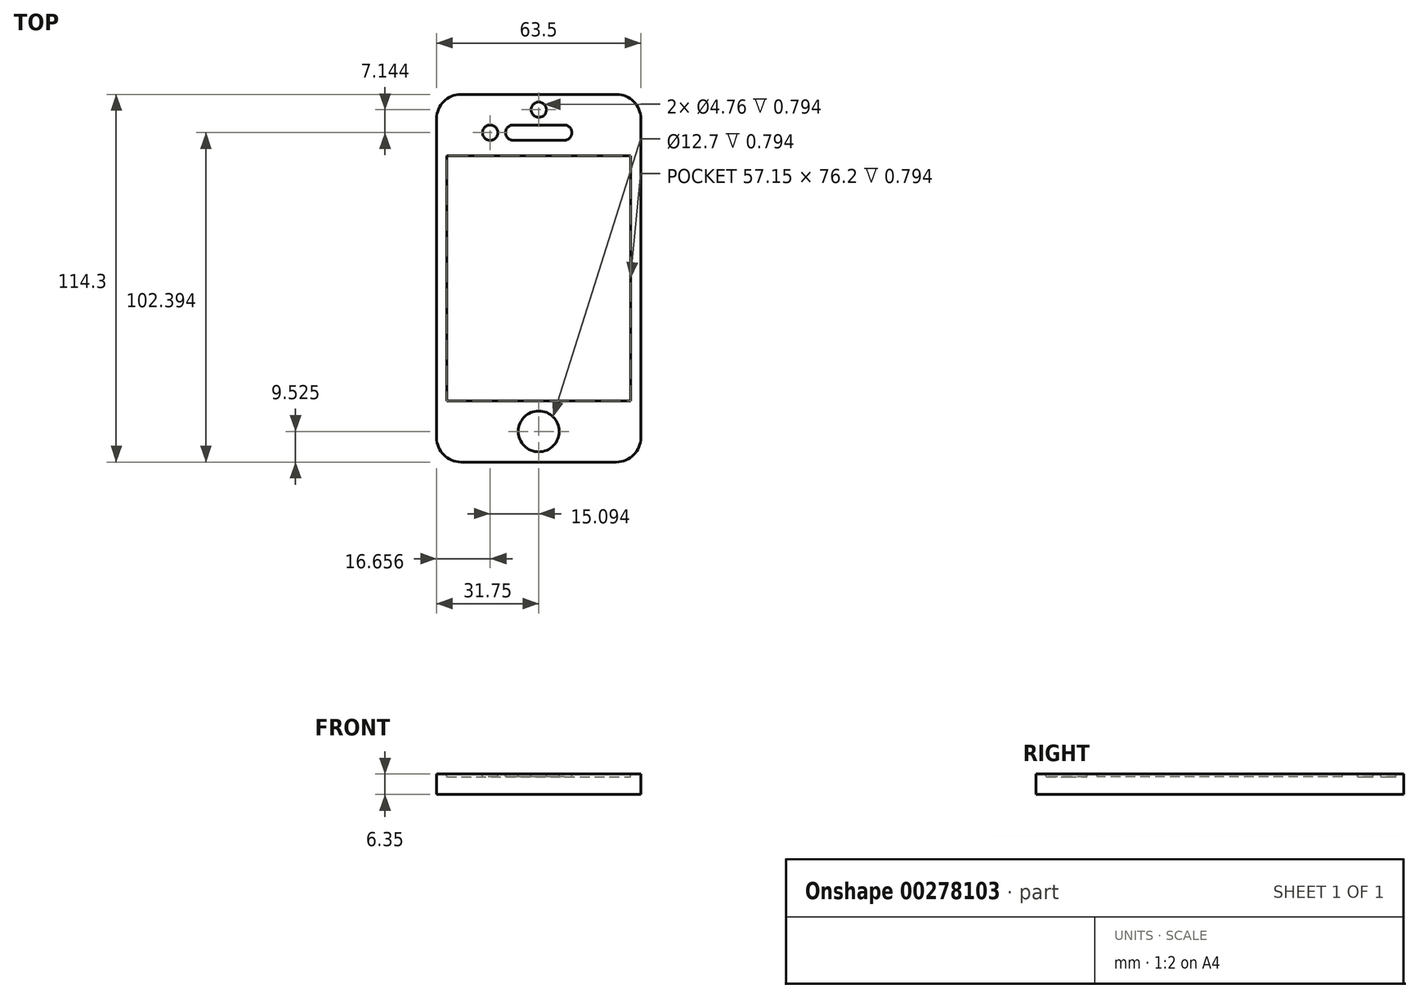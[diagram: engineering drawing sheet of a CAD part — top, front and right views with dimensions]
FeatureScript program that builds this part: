
annotation { "Feature Type Name" : "Feature", "Feature Type Description" : "" }
export const myFeature = defineFeature(function(context is Context, id is Id, definition is map)
    precondition{}
    {
        {
            var Q0;
            Q0=qCreatedBy(makeId("Top.planeOp"),FACE);
            var sketch = newSketch(context, id + "F2", { "sketchPlane" : qUnion([Q0])});
            skLineSegment(sketch, "E0.bottom", {"start": v(24.13, 57.15) * mm, "end": v(-24.13, 57.15) * mm});
            skLineSegment(sketch, "E0.top", {"start": v(24.13, -57.15) * mm, "end": v(-24.13, -57.15) * mm});
            skLineSegment(sketch, "E0.left", {"start": v(31.75, 49.53) * mm, "end": v(31.75, -49.53) * mm});
            skLineSegment(sketch, "E0.right", {"start": v(-31.75, 49.53) * mm, "end": v(-31.75, -49.53) * mm});
            skPoint(sketch, "E0.middle", {"position": v(0, 0) * mm});
            skPoint(sketch, "E1.visualSharp", {"position": v(-31.75, 57.15) * mm});
            skArc(sketch, "E1.filletArc", {"start": v(-24.13, 57.15) * mm, "mid": v(-29.52, 54.92) * mm, "end": v(-31.75, 49.53) * mm});
            skPoint(sketch, "E2.visualSharp", {"position": v(31.75, 57.15) * mm});
            skArc(sketch, "E2.filletArc", {"start": v(31.75, 49.53) * mm, "mid": v(29.52, 54.92) * mm, "end": v(24.13, 57.15) * mm});
            skPoint(sketch, "E3.visualSharp", {"position": v(-31.75, -57.15) * mm});
            skArc(sketch, "E3.filletArc", {"start": v(-31.75, -49.53) * mm, "mid": v(-29.52, -54.92) * mm, "end": v(-24.13, -57.15) * mm});
            skPoint(sketch, "E4.visualSharp", {"position": v(31.75, -57.15) * mm});
            skArc(sketch, "E4.filletArc", {"start": v(24.13, -57.15) * mm, "mid": v(29.52, -54.92) * mm, "end": v(31.75, -49.53) * mm});
            skSolve(sketch);
        }
        {
            var Q0;
            Q0 = qSketchRegion(id + "F2", true);
            extrude(context, id + "F3", {"entities" : qUnion([Q0]), "depth" : 6.35 * mm});
        }
        {
            var Q0;
            Q0=makeQuery(id+"F3.opExtrude","CAP_FACE",FACE,{"disambiguationData":[OSD([sQuery(id+"F2.wireOp",EDGE,"E0.bottom"),sQuery(id+"F2.wireOp",EDGE,"E0.top"),sQuery(id+"F2.wireOp",EDGE,"E0.left"),sQuery(id+"F2.wireOp",EDGE,"E0.right"),sQuery(id+"F2.wireOp",EDGE,"E1.filletArc"),sQuery(id+"F2.wireOp",EDGE,"E2.filletArc"),sQuery(id+"F2.wireOp",EDGE,"E3.filletArc"),sQuery(id+"F2.wireOp",EDGE,"E4.filletArc")])],"isStart":false});
            var sketch = newSketch(context, id + "F0", { "sketchPlane" : qUnion([Q0])});
            skCircle(sketch, "E5", {"center": v(0, -47.63) * mm, "radius": 6.35 * mm});
            skLineSegment(sketch, "E6", {"start": v(-7.94, 42.86) * mm, "end": v(7.94, 42.86) * mm});
            skLineSegment(sketch, "E7", {"start": v(7.94, 47.63) * mm, "end": v(-7.94, 47.63) * mm});
            skArc(sketch, "E8", {"start": v(-7.94, 47.62) * mm, "mid": v(-10.32, 45.24) * mm, "end": v(-7.94, 42.86) * mm});
            skArc(sketch, "E9", {"start": v(7.94, 42.86) * mm, "mid": v(10.32, 45.24) * mm, "end": v(7.94, 47.63) * mm});
            skPoint(sketch, "E10", {"position": v(0, 42.86) * mm});
            skLineSegment(sketch, "E11.bottom", {"start": v(-28.57, 38.1) * mm, "end": v(28.57, 38.1) * mm});
            skLineSegment(sketch, "E11.top", {"start": v(-28.57, -38.1) * mm, "end": v(28.58, -38.1) * mm});
            skLineSegment(sketch, "E11.left", {"start": v(-28.57, 38.1) * mm, "end": v(-28.58, -38.1) * mm});
            skLineSegment(sketch, "E11.right", {"start": v(28.58, 38.1) * mm, "end": v(28.57, -38.1) * mm});
            skPoint(sketch, "E12", {"position": v(0, 38.1) * mm});
            skPoint(sketch, "E13", {"position": v(-28.58, 0) * mm});
            skCircle(sketch, "E14", {"center": v(-15.1, 45.24) * mm, "radius": 2.38 * mm});
            skCircle(sketch, "E15", {"center": v(0, 52.39) * mm, "radius": 2.38 * mm});
            skSolve(sketch);
        }
        {
            var Q0;
            Q0 = qSketchRegion(id + "F0", true);
            extrude(context, id + "F1", {"entities" : qUnion([Q0]), "operationType" : NewBodyOperationType.REMOVE, "oppositeDirection" : true, "depth" : 0.8 * mm});
        }
    });
